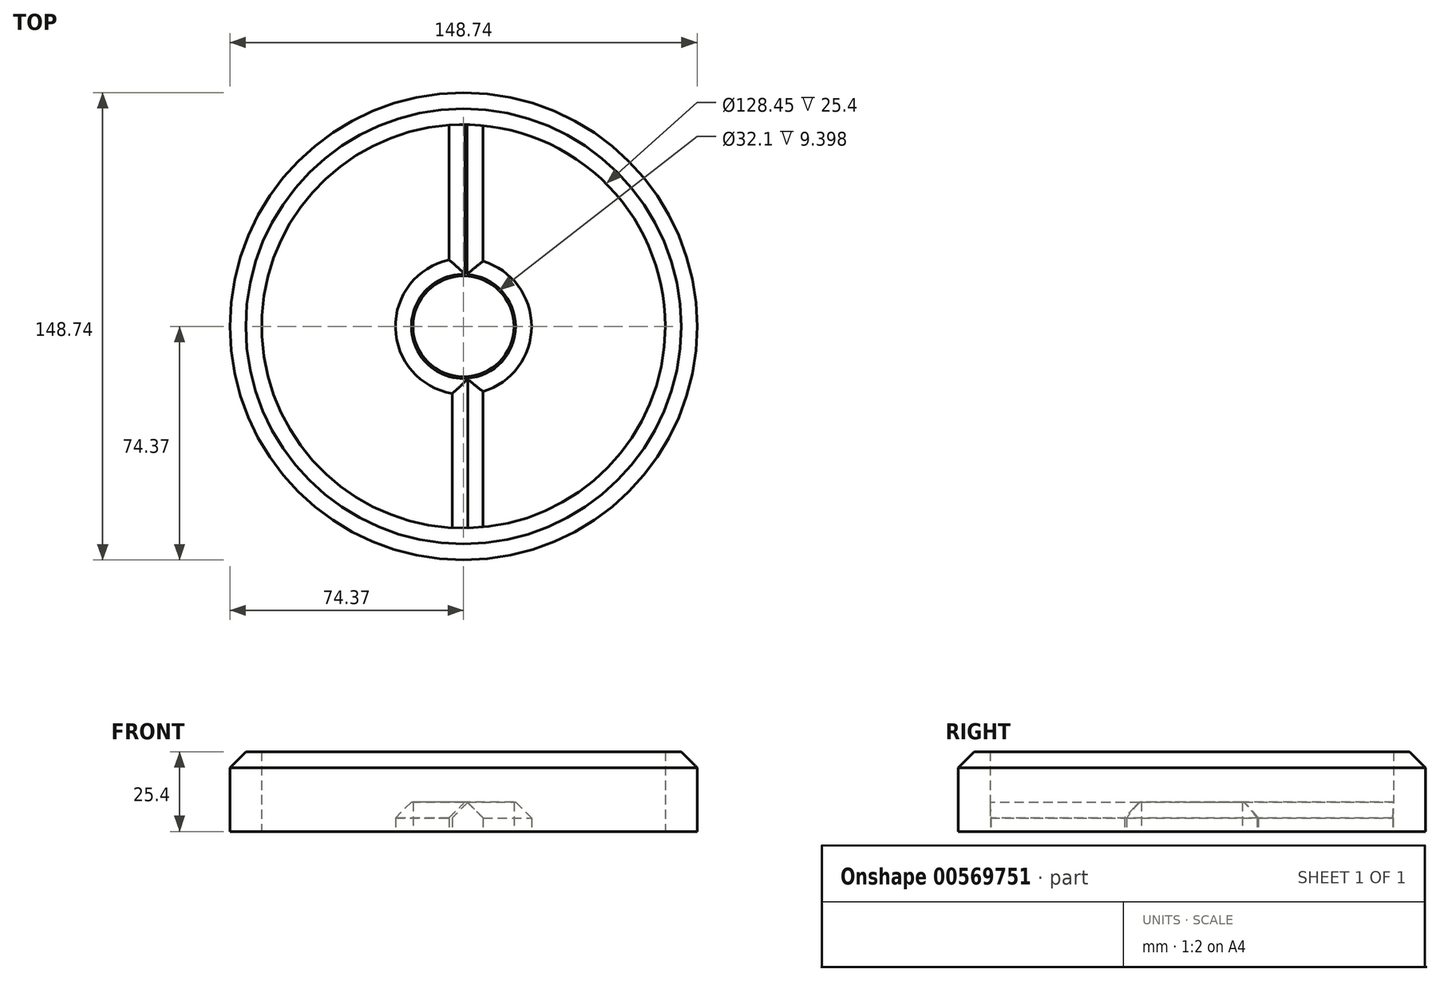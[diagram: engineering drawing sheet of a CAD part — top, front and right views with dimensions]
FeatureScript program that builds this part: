
annotation { "Feature Type Name" : "Feature", "Feature Type Description" : "" }
export const myFeature = defineFeature(function(context is Context, id is Id, definition is map)
    precondition{}
    {
        {
            var Q0;
            Q0=qCreatedBy(makeId("Top.planeOp"),FACE);
            var sketch = newSketch(context, id + "F0", { "sketchPlane" : qUnion([Q0])});
            skCircle(sketch, "E0", {"center": v(0, 0) * mm, "radius": 74.37 * mm});
            skCircle(sketch, "E1", {"center": v(0, 0) * mm, "radius": 64.22 * mm});
            skSolve(sketch);
        }
        {
            var Q0;
            Q0=qCreatedBy(makeId("Top.planeOp"),FACE);
            var sketch = newSketch(context, id + "F1", { "sketchPlane" : qUnion([Q0])});
            skCircle(sketch, "E2", {"center": v(0, 0) * mm, "radius": 21.66 * mm});
            skCircle(sketch, "E3", {"center": v(0, 0) * mm, "radius": 16.05 * mm});
            skSolve(sketch);
        }
        {
            var Q0;
            Q0=qCreatedBy(makeId("Top.planeOp"),FACE);
            var sketch = newSketch(context, id + "F2", { "sketchPlane" : qUnion([Q0])});
            skLineSegment(sketch, "E4.bottom", {"start": v(6.24, -68.16) * mm, "end": v(-3.6, -68.16) * mm});
            skLineSegment(sketch, "E4.top", {"start": v(6.24, -18.44) * mm, "end": v(-3.6, -18.44) * mm});
            skLineSegment(sketch, "E4.left", {"start": v(6.24, -68.16) * mm, "end": v(6.24, -18.44) * mm});
            skLineSegment(sketch, "E4.right", {"start": v(-3.6, -68.16) * mm, "end": v(-3.6, -18.44) * mm});
            skLineSegment(sketch, "E5.bottom", {"start": v(-4.62, 18.32) * mm, "end": v(6.24, 18.32) * mm});
            skLineSegment(sketch, "E5.top", {"start": v(-4.62, 68.08) * mm, "end": v(6.24, 68.08) * mm});
            skLineSegment(sketch, "E5.left", {"start": v(-4.62, 18.32) * mm, "end": v(-4.62, 68.08) * mm});
            skLineSegment(sketch, "E5.right", {"start": v(6.24, 18.32) * mm, "end": v(6.24, 68.08) * mm});
            skSolve(sketch);
        }
        {
            var Q0;
            Q0=makeQuery(id+"F0.imprint","IMPRINT",FACE,{"disambiguationData":[TD([[makeQuery(id+"F0.imprint","IMPRINT",EDGE,{"derivedFrom":sQuery(id+"F0.wireOp",EDGE,"E0")}),1.0]])]});
            extrude(context, id + "F3", {"entities" : qUnion([Q0]), "depth" : 25.4 * mm, "offsetDistance" : 25.4 * mm});
        }
        {
            var Q0;
            Q0=makeQuery(id+"F1.imprint","IMPRINT",FACE,{"disambiguationData":[TD([[makeQuery(id+"F1.imprint","IMPRINT",EDGE,{"derivedFrom":sQuery(id+"F1.wireOp",EDGE,"E2")}),1.0]])]});
            var Q1;
            Q1=makeQuery(id+"F2.imprint","IMPRINT",FACE,{"disambiguationData":[TD([[makeQuery(id+"F2.imprint","IMPRINT",EDGE,{"derivedFrom":sQuery(id+"F2.wireOp",EDGE,"E5.bottom")}),1.0]])]});
            var Q2;
            Q2=makeQuery(id+"F2.imprint","IMPRINT",FACE,{"disambiguationData":[TD([[makeQuery(id+"F2.imprint","IMPRINT",EDGE,{"derivedFrom":sQuery(id+"F2.wireOp",EDGE,"E4.bottom")}),-1.0]])]});
            extrude(context, id + "F4", {"entities" : qUnion([Q0, Q1, Q2]), "operationType" : NewBodyOperationType.ADD, "depth" : 9.4 * mm, "offsetDistance" : 25.4 * mm});
        }
        {
            var Q0;
            Q0=makeQuery(id+"F3.opExtrude","CAP_EDGE",EDGE,{"disambiguationData":[OSD([sQuery(id+"F0.wireOp",EDGE,"E0")])],"isStart":false});
            chamfer(context, id + "F5", {"entities" : qUnion([Q0]), "width" : 5.08 * mm, "tangentPropagation" : true});
        }
        {
            var Q0;
            Q0=makeQuery(id+"F4.opExtrude","CAP_EDGE",EDGE,{"disambiguationData":[OSD([sQuery(id+"F2.wireOp",EDGE,"E5.right")])],"isStart":false});
            var Q1;
            Q1=makeQuery(id+"F4.opExtrude","CAP_EDGE",EDGE,{"disambiguationData":[OSD([sQuery(id+"F2.wireOp",EDGE,"E5.left")])],"isStart":false});
            var Q2;
            {var subQ0=sQuery(id+"F2.wireOp",EDGE,"E4.right");var subQ1=sQuery(id+"F1.wireOp",EDGE,"E2");Q2=makeQuery(id+"F4.boolean.opBoolean","SPLIT",EDGE,{"disambiguationData":[TD([makeQuery(id+"F4.opExtrude","SWEPT_FACE",FACE,{"disambiguationData":[OSD([subQ0])]})])],"derivedFrom":makeQuery(id+"F4.opExtrude","CAP_EDGE",EDGE,{"disambiguationData":[OSD([subQ1])],"isStart":false})});}
            var Q3;
            {var subQ0=sQuery(id+"F2.wireOp",EDGE,"E4.left");var subQ1=sQuery(id+"F1.wireOp",EDGE,"E2");Q3=makeQuery(id+"F4.boolean.opBoolean","SPLIT",EDGE,{"disambiguationData":[TD([makeQuery(id+"F4.opExtrude","SWEPT_FACE",FACE,{"disambiguationData":[OSD([subQ0])]})])],"derivedFrom":makeQuery(id+"F4.opExtrude","CAP_EDGE",EDGE,{"disambiguationData":[OSD([subQ1])],"isStart":false})});}
            var Q4;
            Q4=makeQuery(id+"F4.opExtrude","CAP_EDGE",EDGE,{"disambiguationData":[OSD([sQuery(id+"F2.wireOp",EDGE,"E4.right")])],"isStart":false});
            var Q5;
            Q5=makeQuery(id+"F4.opExtrude","CAP_EDGE",EDGE,{"disambiguationData":[OSD([sQuery(id+"F2.wireOp",EDGE,"E4.left")])],"isStart":false});
            chamfer(context, id + "F6", {"entities" : qUnion([Q0, Q1, Q2, Q3, Q4, Q5]), "width" : 5.08 * mm, "tangentPropagation" : true});
        }
    });
